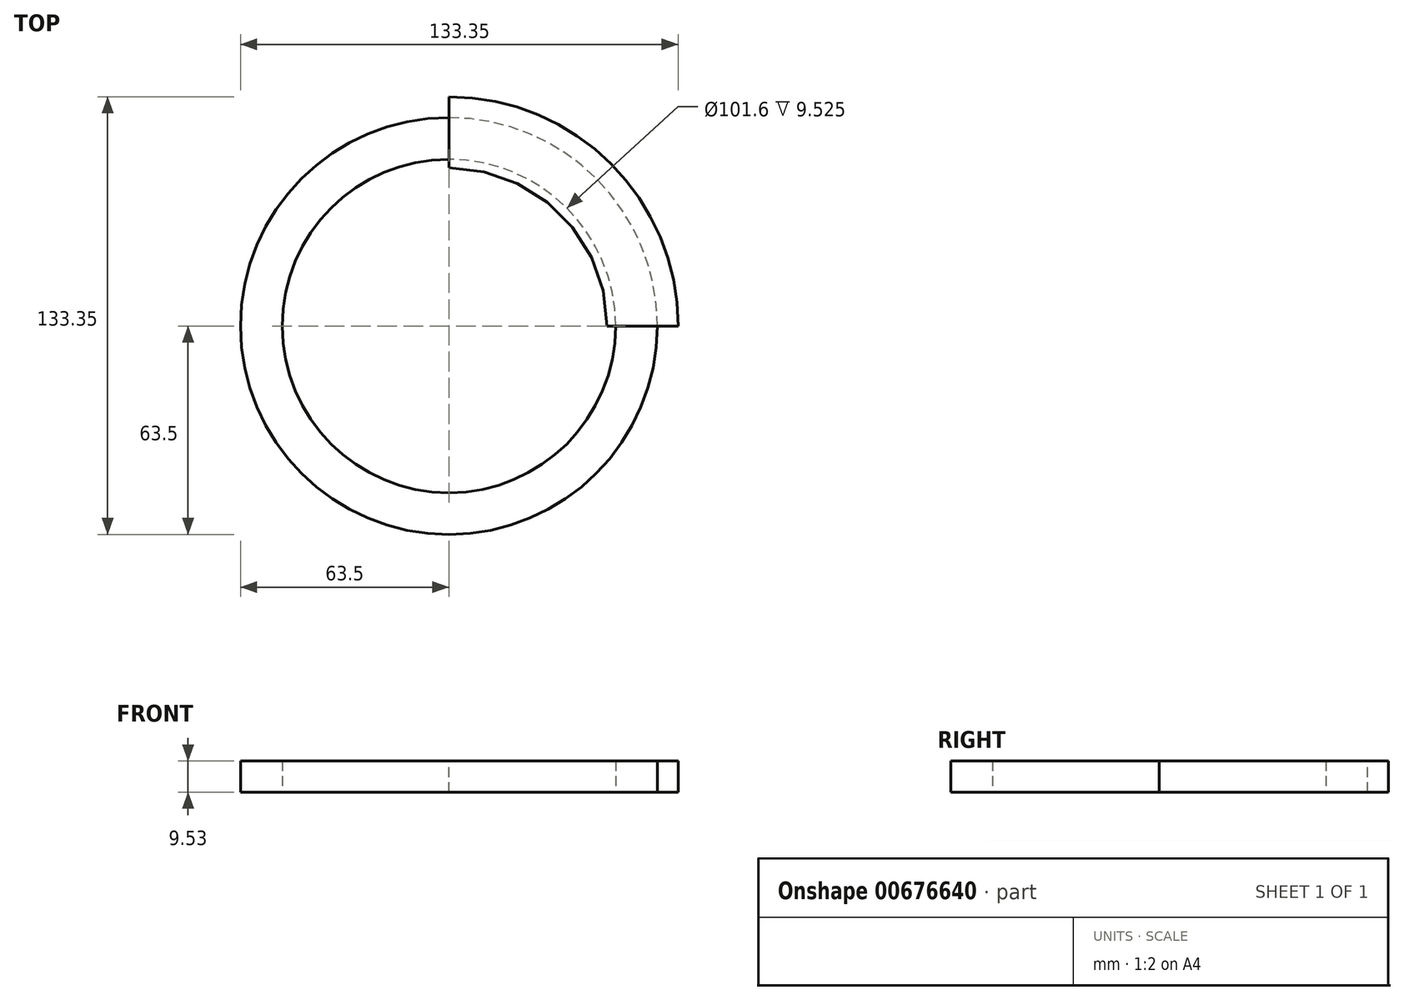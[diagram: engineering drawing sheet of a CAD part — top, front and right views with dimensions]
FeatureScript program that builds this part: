
annotation { "Feature Type Name" : "Feature", "Feature Type Description" : "" }
export const myFeature = defineFeature(function(context is Context, id is Id, definition is map)
    precondition{}
    {
        {
            var Q0;
            Q0=qCreatedBy(makeId("Top.planeOp"),FACE);
            var sketch = newSketch(context, id + "F0", { "sketchPlane" : qUnion([Q0])});
            skCircle(sketch, "E0", {"center": v(0, 0) * mm, "radius": 50.8 * mm});
            skSolve(sketch);
        }
        {
            var Q0;
            Q0=makeQuery(id+"F0.imprint","IMPRINT",FACE,{"disambiguationData":[TD([[makeQuery(id+"F0.imprint","IMPRINT",EDGE,{"derivedFrom":sQuery(id+"F0.wireOp",EDGE,"E0")}),1.0]])]});
            extrude(context, id + "F1", {"entities" : qUnion([Q0]), "depth" : 9.52 * mm, "offsetDistance" : 25.4 * mm});
        }
        {
            var Q0;
            Q0=qCreatedBy(makeId("Top.planeOp"),FACE);
            var sketch = newSketch(context, id + "F2", { "sketchPlane" : qUnion([Q0])});
            skCircle(sketch, "E1", {"center": v(0, 0) * mm, "radius": 63.5 * mm});
            skSolve(sketch);
        }
        {
            var Q0;
            Q0 = qSketchRegion(id + "F2", true);
            extrude(context, id + "F3", {"entities" : qUnion([Q0]), "depth" : 9.52 * mm, "offsetDistance" : 25.4 * mm});
        }
        {
            var Q0;
            Q0=makeQuery(id+"F1.opExtrude","SWEPT_BODY",BODY,{"disambiguationData":[OSD([sQuery(id+"F0.wireOp",EDGE,"E0")])]});
            var Q1;
            Q1=makeQuery(id+"F3.opExtrude","SWEPT_BODY",BODY,{"disambiguationData":[OSD([sQuery(id+"F2.wireOp",EDGE,"E1")])]});
            booleanBodies(context, id + "F4", {"operationType" : BooleanOperationType.SUBTRACTION, "tools" : qUnion([Q0]), "targets" : qUnion([Q1])});
        }
        {
            var Q0;
            Q0=makeQuery(id+"F3.opExtrude","CAP_FACE",FACE,{"disambiguationData":[OSD([sQuery(id+"F2.wireOp",EDGE,"E1")])],"isStart":false});
            var sketch = newSketch(context, id + "F5", { "sketchPlane" : qUnion([Q0])});
            skArc(sketch, "E2", {"start": v(69.85, 0) * mm, "mid": v(49.4, 49.4) * mm, "end": v(0, 69.85) * mm});
            skLineSegment(sketch, "E3", {"start": v(0, 69.85) * mm, "end": v(0, 30.13) * mm});
            skArc(sketch, "E4", {"start": v(0, 30.13) * mm, "mid": v(21.3, 21.3) * mm, "end": v(30.13, 0) * mm});
            skLineSegment(sketch, "E5", {"start": v(30.13, 0) * mm, "end": v(69.85, 0) * mm});
            skArc(sketch, "E6", {"start": v(0, 63.5) * mm, "mid": v(-44.9, -44.9) * mm, "end": v(63.5, 0) * mm, "construction": true});
            skArc(sketch, "E7", {"start": v(63.5, 0) * mm, "mid": v(44.9, 44.9) * mm, "end": v(0, 63.5) * mm});
            skSolve(sketch);
        }
        {
            var Q0;
            {var subQ0=sQuery(id+"F5.wireOp",EDGE,"E2");Q0=makeQuery(id+"F5.imprint","IMPRINT",FACE,{"disambiguationData":[TD([[makeQuery(id+"F5.imprint","IMPRINT",EDGE,{"derivedFrom":subQ0}),1.0]])]});}
            extrude(context, id + "F6", {"entities" : qUnion([Q0]), "oppositeDirection" : true, "depth" : 9.52 * mm, "offsetDistance" : 25.4 * mm});
        }
        {
            var Q0;
            Q0 = qSketchRegion(id + "F5", true);
            extrude(context, id + "F7", {"entities" : qUnion([Q0]), "depth" : 1 / 203.2 * mm, "offsetDistance" : 25.4 * mm});
        }
        {
            var Q0;
            Q0=makeQuery(id+"F7.opExtrude","CAP_FACE",FACE,{"disambiguationData":[OSD([sQuery(id+"F5.wireOp",EDGE,"E2"),sQuery(id+"F5.wireOp",EDGE,"E3"),sQuery(id+"F5.wireOp",EDGE,"E4"),sQuery(id+"F5.wireOp",EDGE,"E5")])],"isStart":false});
            var sketch = newSketch(context, id + "F8", { "sketchPlane" : qUnion([Q0])});
            skCircle(sketch, "E8.cCircle", {"center": v(0, 0) * mm, "radius": 48.2 * mm, "construction": true});
            skLineSegment(sketch, "E8.0", {"start": v(48.2, 0) * mm, "end": v(47, -10.73) * mm});
            skLineSegment(sketch, "E8.1", {"start": v(47, -10.73) * mm, "end": v(43.43, -20.92) * mm});
            skLineSegment(sketch, "E8.2", {"start": v(43.43, -20.92) * mm, "end": v(37.7, -30.06) * mm});
            skLineSegment(sketch, "E8.3", {"start": v(37.7, -30.06) * mm, "end": v(30.06, -37.7) * mm});
            skLineSegment(sketch, "E8.4", {"start": v(30.06, -37.7) * mm, "end": v(20.92, -43.43) * mm});
            skLineSegment(sketch, "E8.5", {"start": v(20.92, -43.43) * mm, "end": v(10.73, -47) * mm});
            skLineSegment(sketch, "E8.6", {"start": v(10.73, -47) * mm, "end": v(0, -48.2) * mm});
            skLineSegment(sketch, "E8.7", {"start": v(0, -48.2) * mm, "end": v(-10.73, -47) * mm});
            skLineSegment(sketch, "E8.8", {"start": v(-10.73, -47) * mm, "end": v(-20.92, -43.43) * mm});
            skLineSegment(sketch, "E8.9", {"start": v(-20.92, -43.43) * mm, "end": v(-30.06, -37.7) * mm});
            skLineSegment(sketch, "E8.10", {"start": v(-30.06, -37.7) * mm, "end": v(-37.7, -30.06) * mm});
            skLineSegment(sketch, "E8.11", {"start": v(-37.7, -30.06) * mm, "end": v(-43.43, -20.92) * mm});
            skLineSegment(sketch, "E8.12", {"start": v(-43.43, -20.92) * mm, "end": v(-47, -10.73) * mm});
            skLineSegment(sketch, "E8.13", {"start": v(-47, -10.73) * mm, "end": v(-48.2, 0) * mm});
            skLineSegment(sketch, "E8.14", {"start": v(-48.2, 0) * mm, "end": v(-47, 10.73) * mm});
            skLineSegment(sketch, "E8.15", {"start": v(-47, 10.73) * mm, "end": v(-43.43, 20.92) * mm});
            skLineSegment(sketch, "E8.16", {"start": v(-43.43, 20.92) * mm, "end": v(-37.7, 30.06) * mm});
            skLineSegment(sketch, "E8.17", {"start": v(-37.7, 30.06) * mm, "end": v(-30.06, 37.7) * mm});
            skLineSegment(sketch, "E8.18", {"start": v(-30.06, 37.7) * mm, "end": v(-20.92, 43.43) * mm});
            skLineSegment(sketch, "E8.19", {"start": v(-20.92, 43.43) * mm, "end": v(-10.73, 47) * mm});
            skLineSegment(sketch, "E8.20", {"start": v(-10.73, 47) * mm, "end": v(0, 48.2) * mm});
            skLineSegment(sketch, "E8.21", {"start": v(0, 48.2) * mm, "end": v(10.73, 47) * mm});
            skLineSegment(sketch, "E8.22", {"start": v(10.73, 47) * mm, "end": v(20.92, 43.43) * mm});
            skLineSegment(sketch, "E8.23", {"start": v(20.92, 43.43) * mm, "end": v(30.06, 37.7) * mm});
            skLineSegment(sketch, "E8.24", {"start": v(30.06, 37.7) * mm, "end": v(37.7, 30.06) * mm});
            skLineSegment(sketch, "E8.25", {"start": v(37.7, 30.06) * mm, "end": v(43.43, 20.92) * mm});
            skLineSegment(sketch, "E8.26", {"start": v(43.43, 20.92) * mm, "end": v(47, 10.73) * mm});
            skLineSegment(sketch, "E8.27", {"start": v(47, 10.73) * mm, "end": v(48.2, 0) * mm});
            skSolve(sketch);
        }
        {
            var Q0;
            Q0 = qSketchRegion(id + "F8", true);
            extrude(context, id + "F9", {"entities" : qUnion([Q0]), "operationType" : NewBodyOperationType.REMOVE, "oppositeDirection" : true, "depth" : 25.4 * mm, "offsetDistance" : 25.4 * mm});
        }
    });
